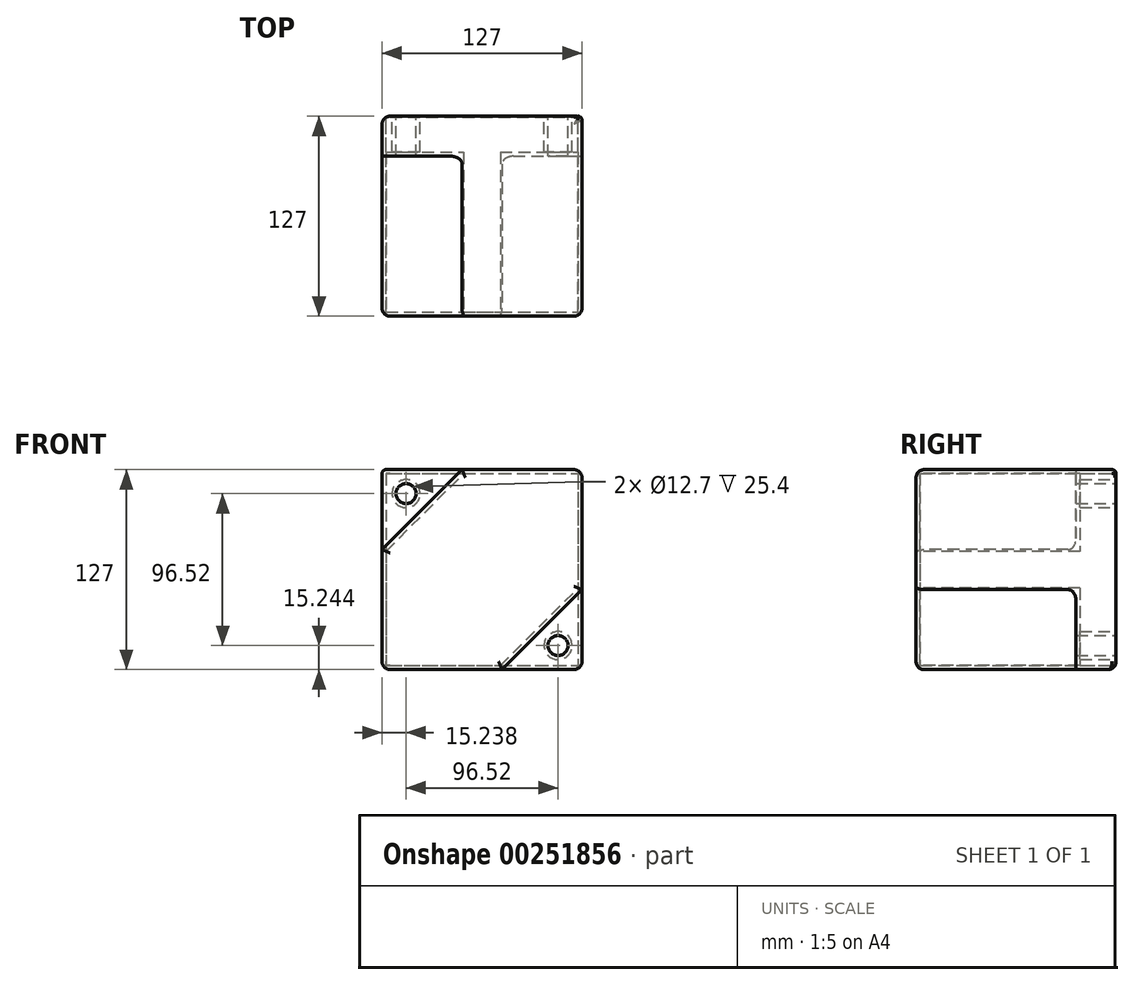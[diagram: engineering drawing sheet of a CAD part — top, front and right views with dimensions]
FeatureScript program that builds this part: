
annotation { "Feature Type Name" : "Feature", "Feature Type Description" : "" }
export const myFeature = defineFeature(function(context is Context, id is Id, definition is map)
    precondition{}
    {
        {
            var Q0;
            Q0=qCreatedBy(makeId("Front.planeOp"),FACE);
            var sketch = newSketch(context, id + "F0", { "sketchPlane" : qUnion([Q0])});
            skLineSegment(sketch, "E0.bottom", {"start": v(-88.65, 93.07) * mm, "end": v(38.35, 93.07) * mm});
            skLineSegment(sketch, "E0.top", {"start": v(-88.65, -33.93) * mm, "end": v(38.35, -33.93) * mm});
            skLineSegment(sketch, "E0.left", {"start": v(-88.65, 93.07) * mm, "end": v(-88.65, -33.93) * mm});
            skLineSegment(sketch, "E0.right", {"start": v(38.35, 93.07) * mm, "end": v(38.35, -33.93) * mm});
            skSolve(sketch);
        }
        {
            var Q0;
            Q0=makeQuery(id+"F0.imprint","IMPRINT",FACE,{"disambiguationData":[TD([[makeQuery(id+"F0.imprint","IMPRINT",EDGE,{"derivedFrom":sQuery(id+"F0.wireOp",EDGE,"E0.bottom")}),-1.0]])]});
            extrude(context, id + "F1", {"entities" : qUnion([Q0]), "depth" : 127 * mm});
        }
        {
            var Q0;
            Q0=makeQuery(id+"F1.opExtrude","CAP_FACE",FACE,{"disambiguationData":[OSD([sQuery(id+"F0.wireOp",EDGE,"E0.bottom"),sQuery(id+"F0.wireOp",EDGE,"E0.top"),sQuery(id+"F0.wireOp",EDGE,"E0.left"),sQuery(id+"F0.wireOp",EDGE,"E0.right")])],"isStart":false});
            var sketch = newSketch(context, id + "F2", { "sketchPlane" : qUnion([Q0])});
            skLineSegment(sketch, "E1", {"start": v(-88.65, 42.27) * mm, "end": v(-37.85, 93.07) * mm});
            skLineSegment(sketch, "E2", {"start": v(-88.65, 42.27) * mm, "end": v(-88.65, 93.07) * mm});
            skLineSegment(sketch, "E3", {"start": v(-88.65, 93.07) * mm, "end": v(-37.85, 93.07) * mm});
            skLineSegment(sketch, "E4", {"start": v(-12.45, -33.93) * mm, "end": v(38.35, 16.87) * mm});
            skLineSegment(sketch, "E5", {"start": v(38.35, 16.87) * mm, "end": v(38.35, -33.93) * mm});
            skLineSegment(sketch, "E6", {"start": v(38.35, -33.93) * mm, "end": v(-12.45, -33.93) * mm});
            skSolve(sketch);
        }
        {
            var Q0;
            Q0 = qSketchRegion(id + "F2", true);
            extrude(context, id + "F3", {"entities" : qUnion([Q0]), "operationType" : NewBodyOperationType.REMOVE, "oppositeDirection" : true, "depth" : 101.6 * mm});
        }
        {
            var Q0;
            Q0=qCreatedBy(makeId("Front.planeOp"),FACE);
            var sketch = newSketch(context, id + "F4", { "sketchPlane" : qUnion([Q0])});
            skCircle(sketch, "E7", {"center": v(-73.41, 77.83) * mm, "radius": 6.35 * mm});
            skCircle(sketch, "E8", {"center": v(23.1, -18.69) * mm, "radius": 6.35 * mm});
            skSolve(sketch);
        }
        {
            var Q0;
            Q0 = qSketchRegion(id + "F4", true);
            extrude(context, id + "F5", {"entities" : qUnion([Q0]), "operationType" : NewBodyOperationType.REMOVE, "depth" : 200.66 * mm});
        }
        {
            var Q0;
            Q0=makeQuery(id+"F1.opExtrude","CAP_FACE",FACE,{"disambiguationData":[OSD([sQuery(id+"F0.wireOp",EDGE,"E0.bottom"),sQuery(id+"F0.wireOp",EDGE,"E0.top"),sQuery(id+"F0.wireOp",EDGE,"E0.left"),sQuery(id+"F0.wireOp",EDGE,"E0.right")])],"isStart":true});
            shell(context, id + "F6", {"entities" : qUnion([Q0]), "thickness" : 2.54 * mm});
        }
        {
            var Q0;
            Q0=makeQuery(id+"F3.boolean.opBoolean","COPY",EDGE,{"derivedFrom":makeQuery(id+"F3.opExtrude","CAP_EDGE",EDGE,{"disambiguationData":[OSD([sQuery(id+"F2.wireOp",EDGE,"E1")])],"isStart":true})});
            var Q1;
            Q1=makeQuery(id+"F3.boolean.opBoolean","COPY",EDGE,{"derivedFrom":makeQuery(id+"F3.opExtrude","SWEPT_EDGE",EDGE,{"disambiguationData":[OSD([sQuery(id+"F0.wireOp",EDGE,"E0.left"),sQuery(id+"F2.wireOp",EDGE,"E1"),sQuery(id+"F2.wireOp",EDGE,"E2")])]})});
            var Q2;
            Q2=makeQuery(id+"F3.boolean.opBoolean","COPY",EDGE,{"derivedFrom":makeQuery(id+"F3.opExtrude","SWEPT_EDGE",EDGE,{"disambiguationData":[OSD([sQuery(id+"F0.wireOp",EDGE,"E0.bottom"),sQuery(id+"F2.wireOp",EDGE,"E1"),sQuery(id+"F2.wireOp",EDGE,"E3")])]})});
            var Q3;
            Q3=makeQuery(id+"F3.boolean.opBoolean","COPY",EDGE,{"derivedFrom":makeQuery(id+"F3.opExtrude","CAP_EDGE",EDGE,{"disambiguationData":[OSD([sQuery(id+"F2.wireOp",EDGE,"E1")])],"isStart":false})});
            var Q4;
            Q4=makeQuery(id+"F3.boolean.opBoolean","COPY",EDGE,{"derivedFrom":makeQuery(id+"F3.opExtrude","CAP_EDGE",EDGE,{"disambiguationData":[OSD([sQuery(id+"F2.wireOp",EDGE,"E3")])],"isStart":false})});
            var Q5;
            Q5=makeQuery(id+"F1.opExtrude","CAP_EDGE",EDGE,{"disambiguationData":[OSD([sQuery(id+"F0.wireOp",EDGE,"E0.bottom")])],"isStart":false});
            var Q6;
            Q6=makeQuery(id+"F1.opExtrude","CAP_FACE",FACE,{"disambiguationData":[OSD([sQuery(id+"F0.wireOp",EDGE,"E0.bottom"),sQuery(id+"F0.wireOp",EDGE,"E0.top"),sQuery(id+"F0.wireOp",EDGE,"E0.left"),sQuery(id+"F0.wireOp",EDGE,"E0.right")])],"isStart":false});
            fillet(context, id + "F7", {"entities" : qUnion([Q0, Q1, Q2, Q3, Q4, Q5, Q6]), "radius" : 5.08 * mm, "tangentPropagation" : true, "allowEdgeOverflow" : false});
        }
        {
            var Q0;
            Q0=makeQuery(id+"F1.opExtrude","CAP_EDGE",EDGE,{"disambiguationData":[OSD([sQuery(id+"F0.wireOp",EDGE,"E0.top")])],"isStart":true});
            var Q1;
            Q1=makeQuery(id+"F3.boolean.opBoolean","COPY",EDGE,{"derivedFrom":makeQuery(id+"F3.opExtrude","CAP_EDGE",EDGE,{"disambiguationData":[OSD([sQuery(id+"F2.wireOp",EDGE,"E6")])],"isStart":false})});
            var Q2;
            Q2=makeQuery(id+"F1.opExtrude","SWEPT_EDGE",EDGE,{"disambiguationData":[OSD([sQuery(id+"F0.wireOp",EDGE,"E0.top"),sQuery(id+"F0.wireOp",EDGE,"E0.right")])]});
            var Q3;
            Q3=makeQuery(id+"F3.boolean.opBoolean","COPY",EDGE,{"derivedFrom":makeQuery(id+"F3.opExtrude","CAP_EDGE",EDGE,{"disambiguationData":[OSD([sQuery(id+"F2.wireOp",EDGE,"E5")])],"isStart":false})});
            fillet(context, id + "F8", {"entities" : qUnion([Q0, Q1, Q2, Q3]), "radius" : 5.08 * mm, "tangentPropagation" : true, "allowEdgeOverflow" : false});
        }
        {
            var Q0;
            Q0=makeQuery(id+"F3.boolean.opBoolean","COPY",EDGE,{"derivedFrom":makeQuery(id+"F3.opExtrude","CAP_EDGE",EDGE,{"disambiguationData":[OSD([sQuery(id+"F2.wireOp",EDGE,"E4")])],"isStart":false})});
            var Q1;
            Q1=makeQuery(id+"F3.boolean.opBoolean","COPY",EDGE,{"derivedFrom":makeQuery(id+"F3.opExtrude","SWEPT_EDGE",EDGE,{"disambiguationData":[OSD([sQuery(id+"F0.wireOp",EDGE,"E0.top"),sQuery(id+"F2.wireOp",EDGE,"E4"),sQuery(id+"F2.wireOp",EDGE,"E6")])]})});
            var Q2;
            Q2=makeQuery(id+"F3.boolean.opBoolean","COPY",EDGE,{"derivedFrom":makeQuery(id+"F3.opExtrude","SWEPT_EDGE",EDGE,{"disambiguationData":[OSD([sQuery(id+"F0.wireOp",EDGE,"E0.right"),sQuery(id+"F2.wireOp",EDGE,"E4"),sQuery(id+"F2.wireOp",EDGE,"E5")])]})});
            var Q3;
            Q3=makeQuery(id+"F1.opExtrude","SWEPT_EDGE",EDGE,{"disambiguationData":[OSD([sQuery(id+"F0.wireOp",EDGE,"E0.bottom"),sQuery(id+"F0.wireOp",EDGE,"E0.right")])]});
            var Q4;
            Q4=makeQuery(id+"F1.opExtrude","SWEPT_EDGE",EDGE,{"disambiguationData":[OSD([sQuery(id+"F0.wireOp",EDGE,"E0.top"),sQuery(id+"F0.wireOp",EDGE,"E0.left")])]});
            fillet(context, id + "F9", {"entities" : qUnion([Q0, Q1, Q2, Q3, Q4]), "radius" : 5.08 * mm, "tangentPropagation" : true, "allowEdgeOverflow" : false});
        }
        {
            var Q0;
            Q0=makeQuery(id+"F1.opExtrude","SWEPT_EDGE",EDGE,{"disambiguationData":[OSD([sQuery(id+"F0.wireOp",EDGE,"E0.bottom"),sQuery(id+"F0.wireOp",EDGE,"E0.left")])]});
            fillet(context, id + "F10", {"entities" : qUnion([Q0]), "radius" : 2.54 * mm, "tangentPropagation" : true, "allowEdgeOverflow" : false});
        }
    });
